# Revit family: LEGRAND_PRISES_NON_VERROUILLEES_ENCASTREES_IP66_440
name_source: partatom
category: Installations électriques
revit_build: Autodesk Revit 2018 (Build: 20170223_1515(x64)
units: mm (PartAtom-declared; Revit-internal decimal feet)

## family parameters
Conserver l'orientation des annotations = Non
Cote de connecteur circulaire = Utiliser le diamètre
Couper avec des vides une fois chargée = Non
Hôte = Face
Partagée = Non
Point de calcul de pièce = Non
Type d'élément = Normal

## types (4) — shared parameters
Conditions Générale d'Utilisation = https://export.legrand.com
Couleur caractéristique = rouge
Description = Prise au standard international pour montage encastré ou saillie avec accessoire permet la connexion d'appareils de puissance
Elévation par défaut = 1000 mm  [stored 3.28084 ft]
Fabricant = Legrand
Position de la Terre h = 11
Standard CEI ou NFC = CEI
Température maximale d'installation = 40°C
Température maximum d'utilisation = 100°C
Température minimum d'installation = -20°C
Température minimum d'utilisation = -50°C
Tension V = 400 440 V  50 60 Hz  rouge
installation Encastrée E ou Saillie S = encastré et saillie
matériau du boitier = plastique
résistance aux chocs IK = 09
sans halogène = Non
type de raccordement = bornes à vis

## per-type parameters (varying)
| type | Dia bouchon | Intensité A | Modèle | Nombre de pôles | RAY BOUCHON | Ray | classe de protection IP | dIA | entraxe de fixation horizontal mm | entraxe de fixation vertical mm | h1 | hauteur mm | largeur mm | profondeur d'encastrement mm | profondeur mm |
| Socle de tableau Hypra  IP66/67-55   16A   440 V   3P+T   plast | 79 mm | 16 A | 051131 | 4 | 40 mm | 26 mm | IP66/67-55 | 53 mm | 60 mm | 70 mm | 50 mm | 84 mm | 74 mm | 41 mm  [stored 0.134514 ft] | 89 mm  [stored 0.291995 ft] |
| Socle tableau Hypra IP44  16A   3P+N+T   440V   plast | 82 mm | 16 A | 051132 | 5 | 41 mm  [stored 0.134514 ft] | 27 mm | IP44 | 55 mm | 60 mm | 70 mm | 50 mm | 84 mm | 80 mm | 44 mm | 88 mm |
| Socle tableau Hypra    IP66/67-55   32A   3P+T   440V   plast | 89 mm  [stored 0.291995 ft] | 32 A | 058136 | 4 | 45 mm | 30 mm  [stored 0.0984252 ft] | IP66/67-55 | 59 mm | 70 mm | 70 mm | 56 mm | 94 mm | 84 mm | 54 mm | 92 mm |
| Socle tableau Hypra   IP66/67-55   3P+T   63A   440 V plast | 106 mm | 63 A | 058225 | 4 | 53 mm | 35 mm | IP66/67-55 | 71 mm | 77 mm | 85 mm | 64 mm | 106 mm | 106 mm | 85 mm | 164 mm |

note: [stored X ft] marks values corroborated as IEEE doubles in the binary element streams (Revit-internal decimal feet)
